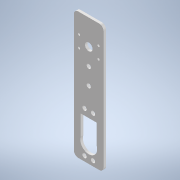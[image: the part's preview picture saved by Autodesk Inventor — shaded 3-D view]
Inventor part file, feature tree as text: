
AUTODESK INVENTOR PART (.ipt)
format: ipt  version: 2021 (Build 250183000, 183)  size: 135,168 bytes
history: native  units: mm
features: extrude x2, sketch x2, other x1
ambient origin geometry x8: Origin, YZ Plane, XZ Plane, XY Plane, X Axis, Y Axis, Z Axis, Center Point
bodies: Body1 (feature_tree)
feature tree (5):
  other  "Sólido1"
  extrude  "Extrusión1"  Depth=10.0mm TaperAngle=0.0deg
  extrude  "Extrusión2"  Depth=0.872665mm
  sketch  "Boceto1"  dims[d29=3.0mm d30=0.0mm d35=10.0mm d36=0.0mm]
  sketch  "Boceto2"  dims[d31=0.5mm d32=0.872665mm]
